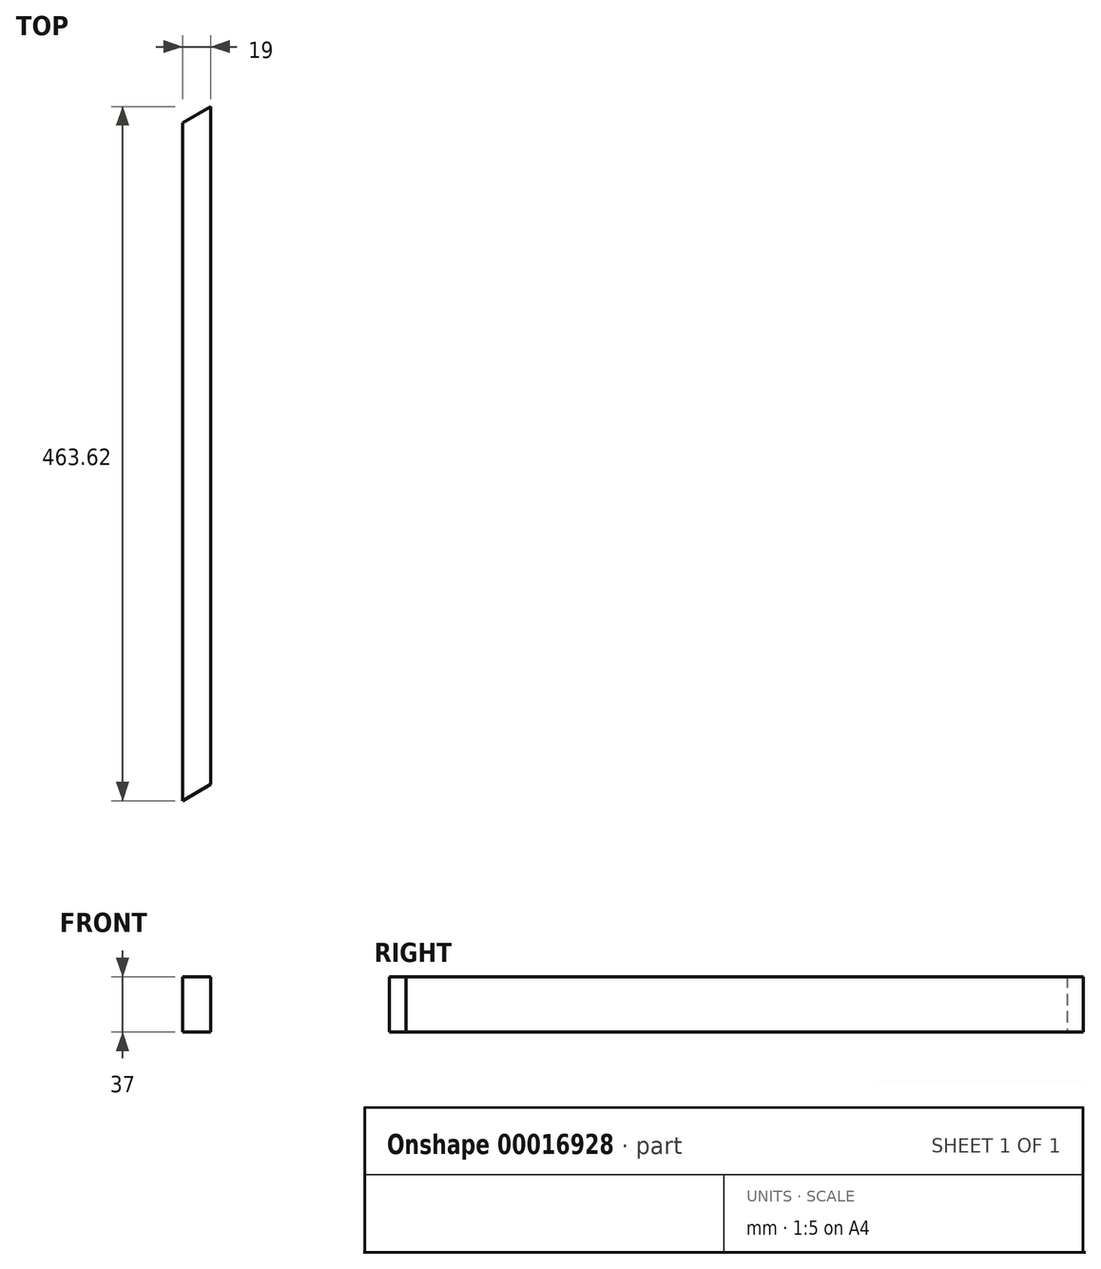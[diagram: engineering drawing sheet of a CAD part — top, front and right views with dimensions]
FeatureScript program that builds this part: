
annotation { "Feature Type Name" : "Feature", "Feature Type Description" : "" }
export const myFeature = defineFeature(function(context is Context, id is Id, definition is map)
    precondition{}
    {
        {
            var Q0;
            Q0=qCreatedBy(makeId("Top.planeOp"),FACE);
            var sketch = newSketch(context, id + "F0", { "sketchPlane" : qUnion([Q0])});
            skLineSegment(sketch, "E0.rect.left", {"start": v(9.5, -220.84) * mm, "end": v(9.5, 231.8) * mm});
            skLineSegment(sketch, "E0.rect.right", {"start": v(-9.5, -231.8) * mm, "end": v(-9.5, 220.84) * mm});
            skPoint(sketch, "E0.rect.middle", {"position": v(0, 0) * mm});
            skLineSegment(sketch, "E1", {"start": v(-9.5, 220.84) * mm, "end": v(9.5, 231.8) * mm});
            skLineSegment(sketch, "E2", {"start": v(-9.5, -231.8) * mm, "end": v(9.5, -220.84) * mm});
            skPoint(sketch, "E3.orphan", {"position": v(9.5, 231.8) * mm});
            skLineSegment(sketch, "E4", {"start": v(9.5, 231.8) * mm, "end": v(-9.5, -231.8) * mm, "construction": true});
            skSolve(sketch);
        }
        {
            var Q0;
            Q0 = qSketchRegion(id + "F0", true);
            extrude(context, id + "F1", {"entities" : qUnion([Q0]), "depth" : 37 * mm});
        }
    });
